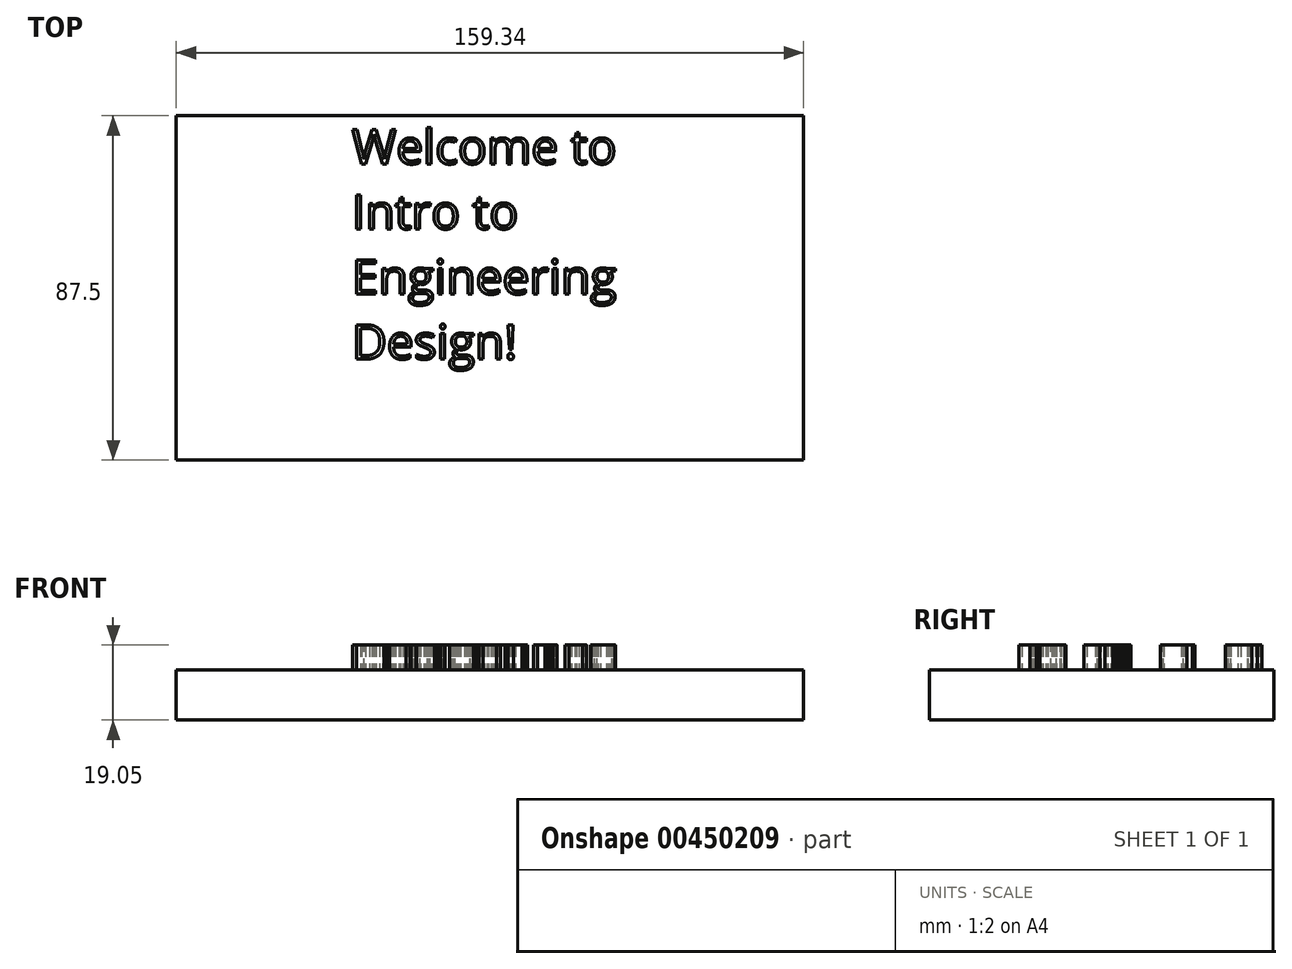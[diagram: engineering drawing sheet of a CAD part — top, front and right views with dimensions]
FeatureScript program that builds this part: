
annotation { "Feature Type Name" : "Feature", "Feature Type Description" : "" }
export const myFeature = defineFeature(function(context is Context, id is Id, definition is map)
    precondition{}
    {
        {
            var Q0;
            Q0=qCreatedBy(makeId("Top.planeOp"),FACE);
            var sketch = newSketch(context, id + "F0", { "sketchPlane" : qUnion([Q0])});
            skLineSegment(sketch, "E0.bottom", {"start": v(-79.67, 43.75) * mm, "end": v(79.67, 43.75) * mm});
            skLineSegment(sketch, "E0.top", {"start": v(-79.67, -43.75) * mm, "end": v(79.67, -43.75) * mm});
            skLineSegment(sketch, "E0.left", {"start": v(-79.67, 43.75) * mm, "end": v(-79.67, -43.75) * mm});
            skLineSegment(sketch, "E0.right", {"start": v(79.67, 43.75) * mm, "end": v(79.67, -43.75) * mm});
            skPoint(sketch, "E0.middle", {"position": v(0, 0) * mm});
            skSolve(sketch);
        }
        {
            var Q0;
            Q0 = qSketchRegion(id + "F0", true);
            extrude(context, id + "F1", {"entities" : qUnion([Q0]), "depth" : 12.7 * mm});
        }
        {
            var Q0;
            Q0=makeQuery(id+"F1.opExtrude","CAP_FACE",FACE,{"disambiguationData":[OSD([sQuery(id+"F0.wireOp",EDGE,"E0.bottom"),sQuery(id+"F0.wireOp",EDGE,"E0.top"),sQuery(id+"F0.wireOp",EDGE,"E0.left"),sQuery(id+"F0.wireOp",EDGE,"E0.right")])],"isStart":false});
            var sketch = newSketch(context, id + "F2", { "sketchPlane" : qUnion([Q0])});
            skText(sketch, "E1", { "text": "Welcome to\nIntro to \nEngineering\nDesign!", "fontName": "OpenSans-Regular.ttf"});
            const initialGuessF2  = {"E1": [-0.03503, 0.03152, 1, 0, 0.00875]};
            skSetInitialGuess(sketch, initialGuessF2);
            skSolve(sketch);
        }
        {
            var Q0;
            Q0 = qSketchRegion(id + "F2", true);
            extrude(context, id + "F3", {"entities" : qUnion([Q0]), "operationType" : NewBodyOperationType.ADD, "depth" : 6.35 * mm});
        }
    });
